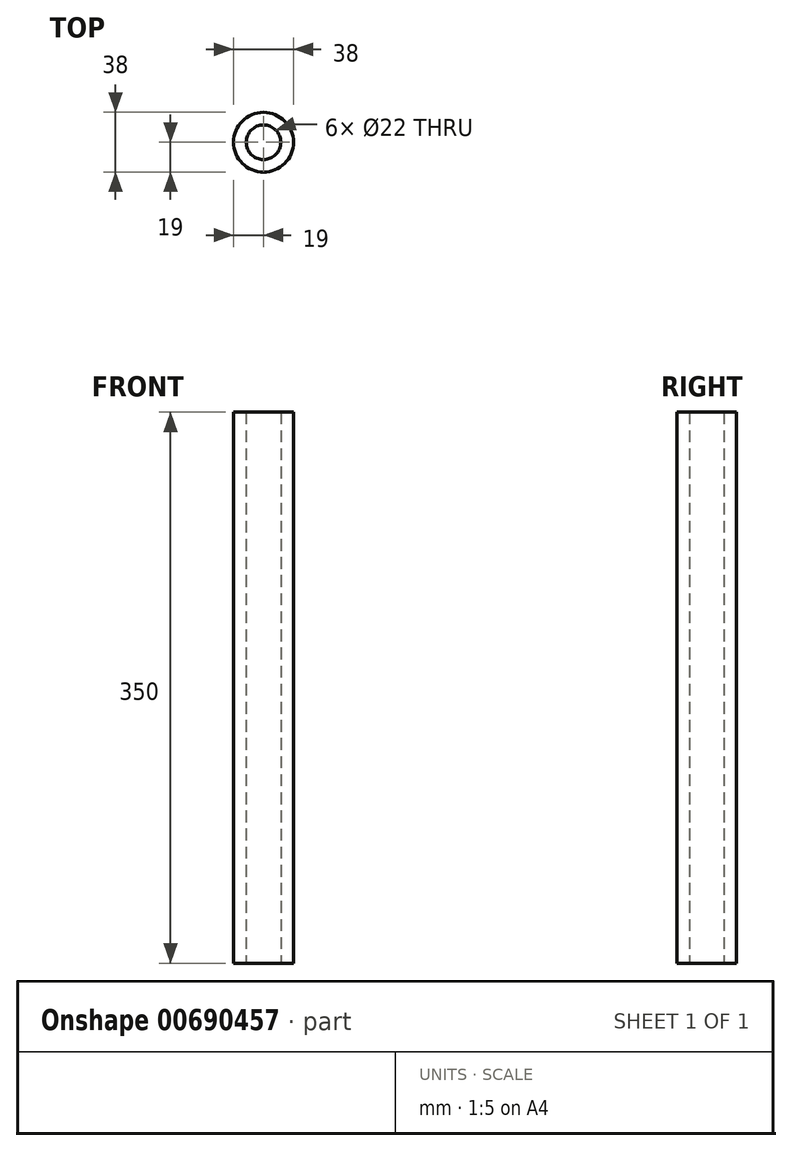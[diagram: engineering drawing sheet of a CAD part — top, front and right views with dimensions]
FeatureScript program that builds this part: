
annotation { "Feature Type Name" : "Feature", "Feature Type Description" : "" }
export const myFeature = defineFeature(function(context is Context, id is Id, definition is map)
    precondition{}
    {
        {
            var Q0;
            Q0=qCreatedBy(makeId("Top.planeOp"),FACE);
            var sketch = newSketch(context, id + "F0", { "sketchPlane" : qUnion([Q0])});
            skCircle(sketch, "E0", {"center": v(0, 0) * mm, "radius": 11 * mm});
            skCircle(sketch, "E1", {"center": v(0, 0) * mm, "radius": 19 * mm});
            skSolve(sketch);
        }
        {
            var Q0;
            Q0=makeQuery(id+"F0.imprint","IMPRINT",FACE,{"disambiguationData":[TD([[makeQuery(id+"F0.imprint","IMPRINT",EDGE,{"derivedFrom":sQuery(id+"F0.wireOp",EDGE,"E0")}),-1.0]])]});
            extrude(context, id + "F1", {"entities" : qUnion([Q0]), "depth" : 350 * mm, "offsetDistance" : 25 * mm});
        }
    });
